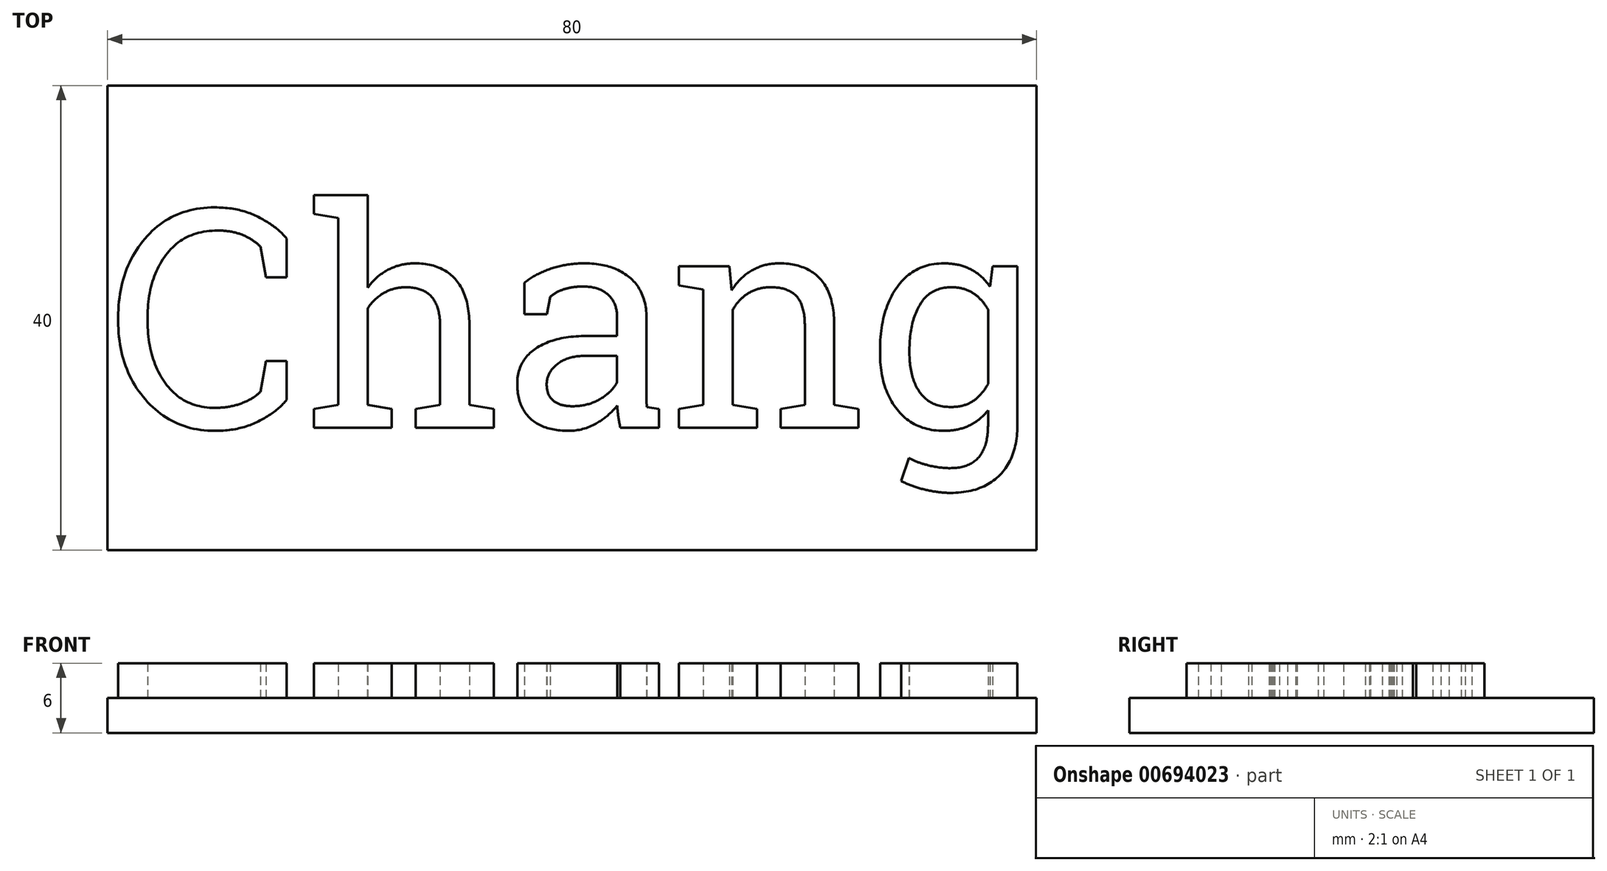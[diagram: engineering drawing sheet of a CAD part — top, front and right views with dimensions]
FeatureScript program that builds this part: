
annotation { "Feature Type Name" : "Feature", "Feature Type Description" : "" }
export const myFeature = defineFeature(function(context is Context, id is Id, definition is map)
    precondition{}
    {
        {
            var Q0;
            Q0=qCreatedBy(makeId("Top.planeOp"),FACE);
            var sketch = newSketch(context, id + "F0", { "sketchPlane" : qUnion([Q0])});
            skLineSegment(sketch, "E0.bottom", {"start": v(40, -20) * mm, "end": v(-40, -20) * mm});
            skLineSegment(sketch, "E0.top", {"start": v(40, 20) * mm, "end": v(-40, 20) * mm});
            skLineSegment(sketch, "E0.left", {"start": v(40, -20) * mm, "end": v(40, 20) * mm});
            skLineSegment(sketch, "E0.right", {"start": v(-40, -20) * mm, "end": v(-40, 20) * mm});
            skPoint(sketch, "E0.middle", {"position": v(0, 0) * mm});
            skSolve(sketch);
        }
        {
            var Q0;
            Q0 = qSketchRegion(id + "F0", true);
            extrude(context, id + "F1", {"entities" : qUnion([Q0]), "depth" : 3 * mm, "offsetDistance" : 25 * mm});
        }
        {
            var Q0;
            Q0=makeQuery(id+"F1.opExtrude","CAP_FACE",FACE,{"disambiguationData":[OSD([sQuery(id+"F0.wireOp",EDGE,"E0.bottom"),sQuery(id+"F0.wireOp",EDGE,"E0.top"),sQuery(id+"F0.wireOp",EDGE,"E0.left"),sQuery(id+"F0.wireOp",EDGE,"E0.right")])],"isStart":false});
            var sketch = newSketch(context, id + "F2", { "sketchPlane" : qUnion([Q0])});
            skText(sketch, "E1", { "text": "Chang", "fontName": "RobotoSlab-Regular.ttf"});
            const initialGuessF2  = {"E1": [-0.04, -0.00947, 1, 0, 0.01894]};
            skSetInitialGuess(sketch, initialGuessF2);
            skSolve(sketch);
        }
        {
            var Q0;
            Q0 = qSketchRegion(id + "F2", true);
            extrude(context, id + "F3", {"entities" : qUnion([Q0]), "operationType" : NewBodyOperationType.ADD, "depth" : 3 * mm, "offsetDistance" : 25 * mm});
        }
    });
